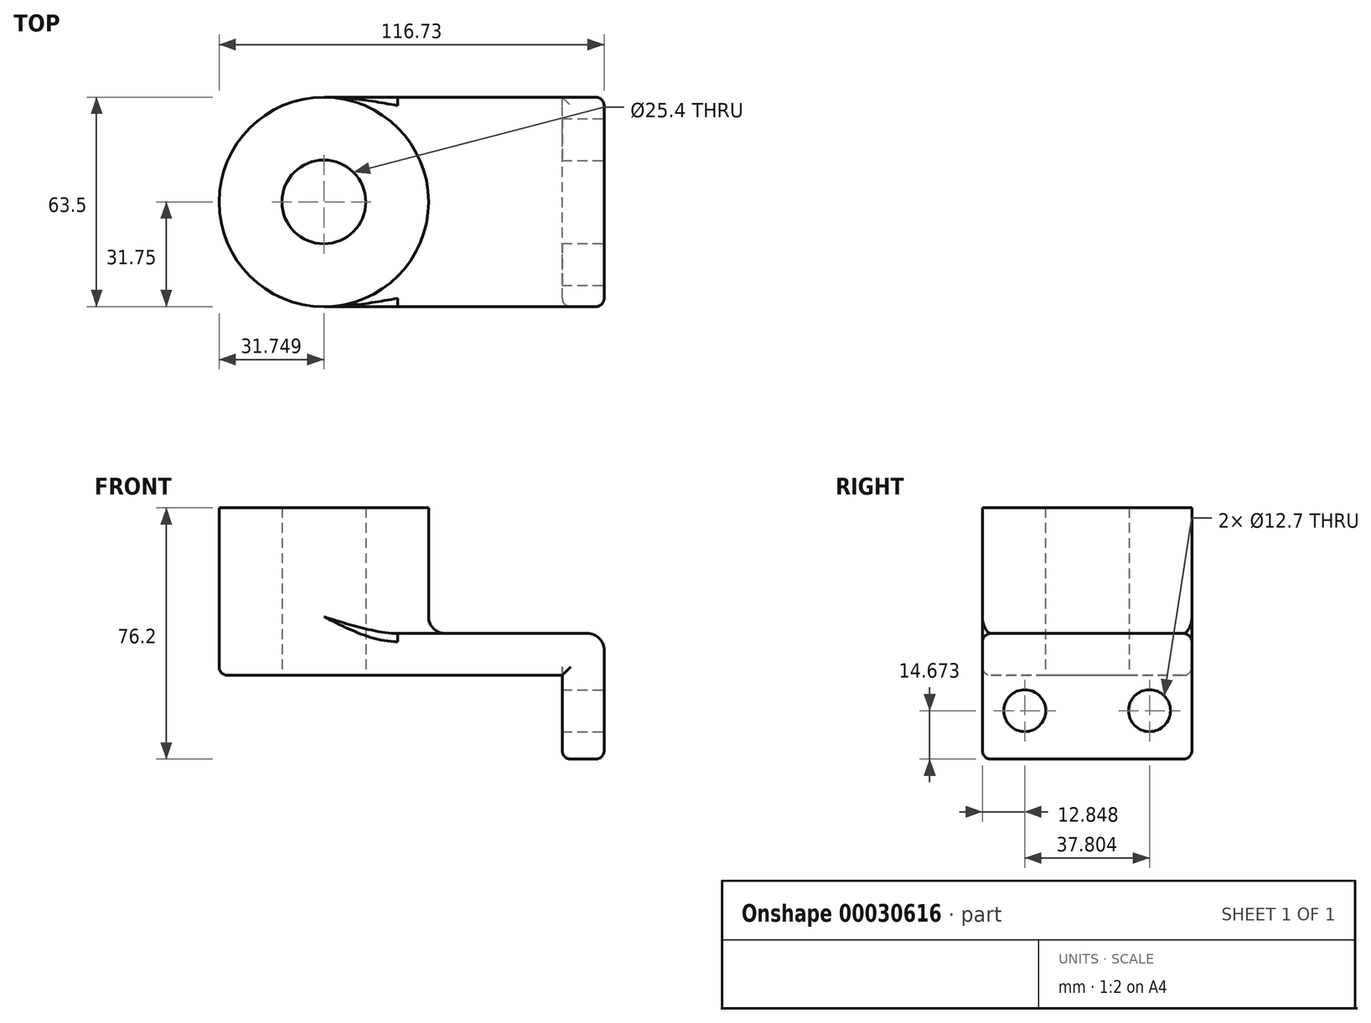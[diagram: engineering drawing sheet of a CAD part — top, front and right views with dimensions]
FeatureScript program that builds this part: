
annotation { "Feature Type Name" : "Feature", "Feature Type Description" : "" }
export const myFeature = defineFeature(function(context is Context, id is Id, definition is map)
    precondition{}
    {
        {
            var Q0;
            Q0=qCreatedBy(makeId("Top.planeOp"),FACE);
            var sketch = newSketch(context, id + "F0", { "sketchPlane" : qUnion([Q0])});
            skLineSegment(sketch, "E0.rect.bottom", {"start": v(-42.5, -31.75) * mm, "end": v(42.5, -31.75) * mm});
            skLineSegment(sketch, "E0.rect.top", {"start": v(-42.5, 31.75) * mm, "end": v(42.5, 31.75) * mm});
            skLineSegment(sketch, "E0.rect.left", {"start": v(-42.5, -31.75) * mm, "end": v(-42.5, 31.75) * mm});
            skLineSegment(sketch, "E0.rect.right", {"start": v(42.5, -31.75) * mm, "end": v(42.5, 31.75) * mm});
            skPoint(sketch, "E0.rect.middle", {"position": v(0, 0) * mm});
            skCircle(sketch, "E1", {"center": v(-42.5, 0) * mm, "radius": 31.75 * mm});
            skCircle(sketch, "E2", {"center": v(-42.5, 0) * mm, "radius": 12.7 * mm});
            skSolve(sketch);
        }
        {
            var Q0;
            Q0 = qSketchRegion(id + "F0", true);
            extrude(context, id + "F1", {"entities" : qUnion([Q0]), "depth" : 12.7 * mm});
        }
        {
            var Q0;
            {var subQ0=sQuery(id+"F0.wireOp",EDGE,"E2");var subQ1=sQuery(id+"F0.wireOp",EDGE,"E0.rect.left");var subQ3=makeQuery(id+"F0.imprint","INTERSECT",VERTEX,{"disambiguationData":[OD(0.0)],"derivedFrom":[subQ1,subQ0]});Q0=makeQuery(id+"F0.imprint","IMPRINT",FACE,{"disambiguationData":[TD([[makeQuery(id+"F0.imprint","IMPRINT",EDGE,{"disambiguationData":[TD([[subQ3,-1.0]])],"derivedFrom":subQ0}),-1.0]])]});}
            var Q1;
            {var subQ0=sQuery(id+"F0.wireOp",EDGE,"E2");var subQ1=sQuery(id+"F0.wireOp",EDGE,"E0.rect.left");var subQ3=makeQuery(id+"F0.imprint","INTERSECT",VERTEX,{"disambiguationData":[OD(0.0)],"derivedFrom":[subQ1,subQ0]});Q1=makeQuery(id+"F0.imprint","IMPRINT",FACE,{"disambiguationData":[TD([[makeQuery(id+"F0.imprint","IMPRINT",EDGE,{"disambiguationData":[TD([[subQ3,1.0]])],"derivedFrom":subQ0}),-1.0]])]});}
            extrude(context, id + "F2", {"entities" : qUnion([Q0, Q1]), "operationType" : NewBodyOperationType.ADD, "depth" : 50.8 * mm});
        }
        {
            var Q0;
            Q0=makeQuery(id+"F1.opExtrude","SWEPT_FACE",FACE,{"disambiguationData":[OSD([sQuery(id+"F0.wireOp",EDGE,"E0.rect.right")])]});
            var sketch = newSketch(context, id + "F3", { "sketchPlane" : qUnion([Q0])});
            skLineSegment(sketch, "E3.bottom", {"start": v(-31.75, 12.7) * mm, "end": v(31.75, 12.7) * mm});
            skLineSegment(sketch, "E3.top", {"start": v(-31.75, -25.4) * mm, "end": v(31.75, -25.4) * mm});
            skLineSegment(sketch, "E3.left", {"start": v(-31.75, 12.7) * mm, "end": v(-31.75, -25.4) * mm});
            skLineSegment(sketch, "E3.right", {"start": v(31.75, 12.7) * mm, "end": v(31.75, -25.4) * mm});
            skCircle(sketch, "E4", {"center": v(-18.9, -10.73) * mm, "radius": 6.35 * mm});
            skLineSegment(sketch, "E5", {"start": v(0, 0) * mm, "end": v(0, -25.4) * mm, "construction": true});
            skCircle(sketch, "E6.MirrorC", {"center": v(18.9, -10.73) * mm, "radius": 6.35 * mm});
            skSolve(sketch);
        }
        {
            var Q0;
            {var subQ2=sQuery(id+"F3.wireOp",EDGE,"E3.top");Q0=makeQuery(id+"F3.imprint","IMPRINT",FACE,{"disambiguationData":[TD([[makeQuery(id+"F3.imprint","IMPRINT",EDGE,{"derivedFrom":subQ2}),1.0]])]});}
            extrude(context, id + "F4", {"entities" : qUnion([Q0]), "operationType" : NewBodyOperationType.ADD, "oppositeDirection" : true, "depth" : 12.7 * mm});
        }
        {
            var Q0;
            {var subQ0=sQuery(id+"F0.wireOp",EDGE,"E1");Q0=makeQuery(id+"F2.boolean.opBoolean","INTERSECT",EDGE,{"derivedFrom":[makeQuery(id+"F1.opExtrude","CAP_FACE",FACE,{"disambiguationData":[OSD([sQuery(id+"F0.wireOp",EDGE,"E0.rect.bottom"),sQuery(id+"F0.wireOp",EDGE,"E0.rect.top"),sQuery(id+"F0.wireOp",EDGE,"E0.rect.right"),subQ0,sQuery(id+"F0.wireOp",EDGE,"E2")])],"isStart":false}),makeQuery(id+"F2.opExtrude","SWEPT_FACE",FACE,{"disambiguationData":[OSD([subQ0])]})]});}
            var Q1;
            Q1=makeQuery(id+"F1.opExtrude","CAP_EDGE",EDGE,{"disambiguationData":[OSD([sQuery(id+"F0.wireOp",EDGE,"E0.rect.right")])],"isStart":false});
            fillet(context, id + "F5", {"entities" : qUnion([Q0, Q1]), "radius" : 5.08 * mm, "tangentPropagation" : true, "allowEdgeOverflow" : false});
        }
        {
            var Q0;
            {var subQ0=sQuery(id+"F0.wireOp",EDGE,"E0.rect.bottom");var subQ1=sQuery(id+"F0.wireOp",EDGE,"E1");Q0=makeQuery(id+"F5.opFillet","BLEND_EDGE",EDGE,{"blendedFrom":[makeQuery(id+"F2.boolean.opBoolean","INTERSECT",EDGE,{"derivedFrom":[makeQuery(id+"F1.opExtrude","CAP_FACE",FACE,{"disambiguationData":[OSD([subQ0,sQuery(id+"F0.wireOp",EDGE,"E0.rect.top"),sQuery(id+"F0.wireOp",EDGE,"E0.rect.right"),subQ1,sQuery(id+"F0.wireOp",EDGE,"E2")])],"isStart":false}),makeQuery(id+"F2.opExtrude","SWEPT_FACE",FACE,{"disambiguationData":[OSD([subQ1])]})]}),makeQuery(id+"F4.boolean.opBoolean","MERGE",FACE,{"derivedFrom":[makeQuery(id+"F1.opExtrude","SWEPT_FACE",FACE,{"disambiguationData":[OSD([subQ0])]}),makeQuery(id+"F4.opExtrude","SWEPT_FACE",FACE,{"disambiguationData":[OSD([sQuery(id+"F3.wireOp",EDGE,"E3.left")])]})]})],"blendedInto":[makeQuery(id+"F4.boolean.opBoolean","MERGE",FACE,{"derivedFrom":[makeQuery(id+"F1.opExtrude","SWEPT_FACE",FACE,{"disambiguationData":[OSD([subQ0])]}),makeQuery(id+"F4.opExtrude","SWEPT_FACE",FACE,{"disambiguationData":[OSD([sQuery(id+"F3.wireOp",EDGE,"E3.left")])]})]})]});}
            var Q1;
            Q1=makeQuery(id+"F1.opExtrude","CAP_EDGE",EDGE,{"disambiguationData":[OSD([sQuery(id+"F0.wireOp",EDGE,"E0.rect.bottom")])],"isStart":false});
            var Q2;
            Q2=makeQuery(id+"F1.opExtrude","CAP_EDGE",EDGE,{"disambiguationData":[OSD([sQuery(id+"F0.wireOp",EDGE,"E0.rect.bottom")])],"isStart":true});
            var Q3;
            Q3=makeQuery(id+"F4.opExtrude","CAP_EDGE",EDGE,{"disambiguationData":[OSD([sQuery(id+"F3.wireOp",EDGE,"E3.left")])],"isStart":false});
            var Q4;
            Q4=makeQuery(id+"F4.opExtrude","SWEPT_EDGE",EDGE,{"disambiguationData":[OSD([sQuery(id+"F3.wireOp",EDGE,"E3.top"),sQuery(id+"F3.wireOp",EDGE,"E3.left")])]});
            var Q5;
            Q5=makeQuery(id+"F4.opExtrude","CAP_EDGE",EDGE,{"disambiguationData":[OSD([sQuery(id+"F0.wireOp",EDGE,"E0.rect.right")])],"isStart":false});
            var Q6;
            Q6=makeQuery(id+"F4.opExtrude","CAP_EDGE",EDGE,{"disambiguationData":[OSD([sQuery(id+"F3.wireOp",EDGE,"E3.top")])],"isStart":false});
            var Q7;
            Q7=makeQuery(id+"F4.opExtrude","CAP_EDGE",EDGE,{"disambiguationData":[OSD([sQuery(id+"F3.wireOp",EDGE,"E3.top")])],"isStart":true});
            var Q8;
            Q8=makeQuery(id+"F4.opExtrude","SWEPT_EDGE",EDGE,{"disambiguationData":[OSD([sQuery(id+"F3.wireOp",EDGE,"E3.top"),sQuery(id+"F3.wireOp",EDGE,"E3.right")])]});
            var Q9;
            Q9=makeQuery(id+"F4.boolean.opBoolean","MERGE",EDGE,{"derivedFrom":[makeQuery(id+"F1.opExtrude","SWEPT_EDGE",EDGE,{"disambiguationData":[OSD([sQuery(id+"F0.wireOp",EDGE,"E0.rect.top"),sQuery(id+"F0.wireOp",EDGE,"E0.rect.right")])]}),makeQuery(id+"F4.opExtrude","CAP_EDGE",EDGE,{"disambiguationData":[OSD([sQuery(id+"F3.wireOp",EDGE,"E3.right")])],"isStart":true})]});
            var Q10;
            Q10=makeQuery(id+"F1.opExtrude","CAP_EDGE",EDGE,{"disambiguationData":[OSD([sQuery(id+"F0.wireOp",EDGE,"E0.rect.top")])],"isStart":true});
            fillet(context, id + "F6", {"entities" : qUnion([Q0, Q1, Q2, Q3, Q4, Q5, Q6, Q7, Q8, Q9, Q10]), "radius" : 2.54 * mm, "tangentPropagation" : true, "allowEdgeOverflow" : false});
        }
    });
